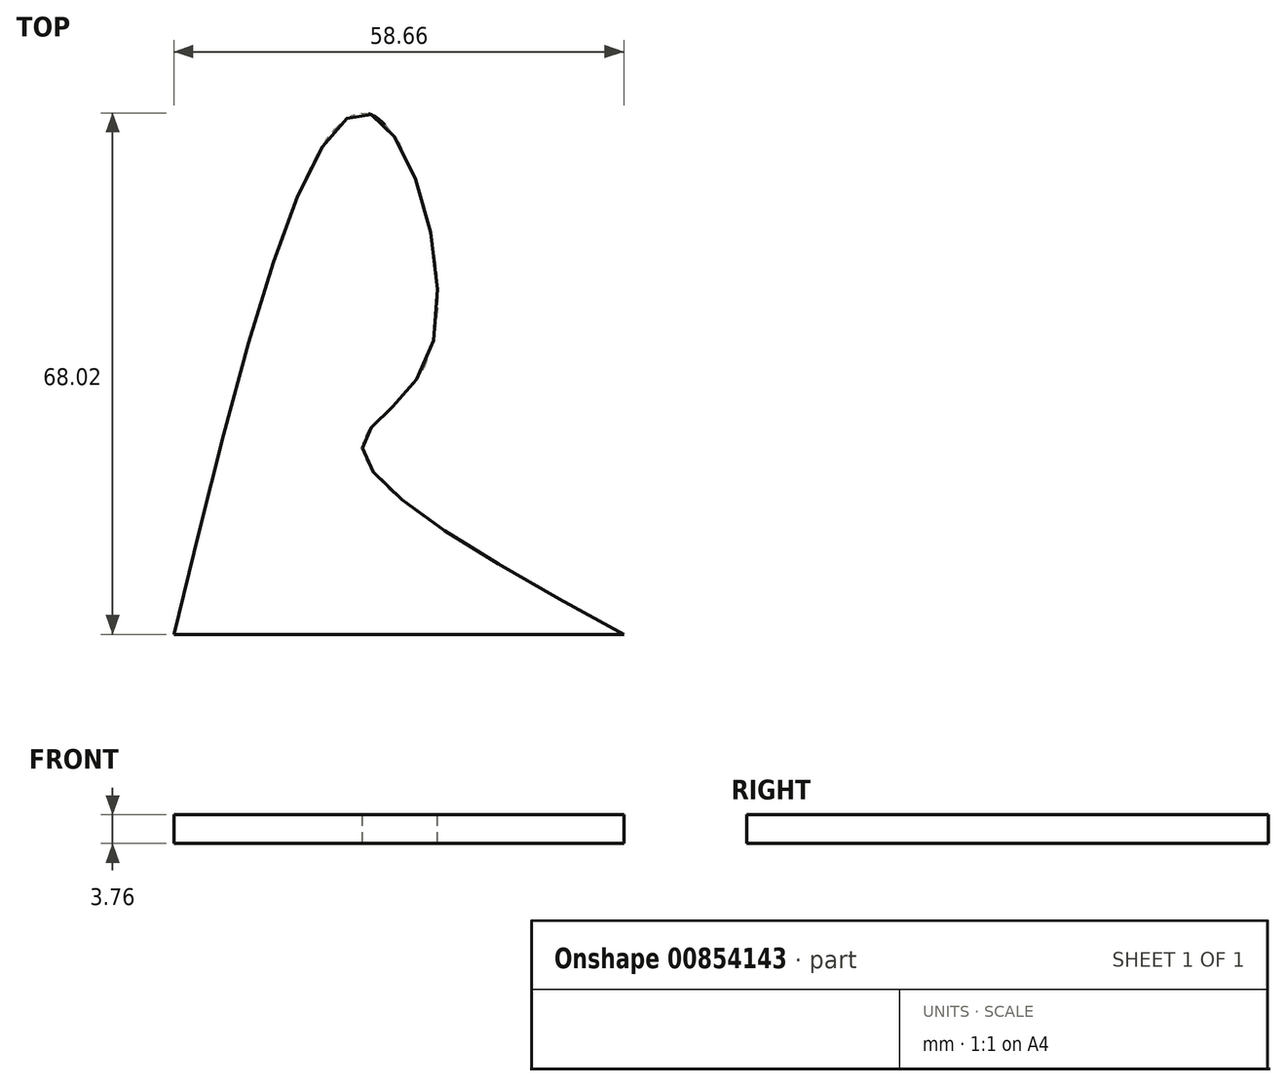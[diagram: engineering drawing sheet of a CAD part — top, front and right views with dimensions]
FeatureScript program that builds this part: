
annotation { "Feature Type Name" : "Feature", "Feature Type Description" : "" }
export const myFeature = defineFeature(function(context is Context, id is Id, definition is map)
    precondition{}
    {
        {
            var Q0;
            Q0=qCreatedBy(makeId("Top.planeOp"),FACE);
            var sketch = newSketch(context, id + "F0", { "sketchPlane" : qUnion([Q0])});
            skLineSegment(sketch, "E0", {"start": v(-58.66, -79.08) * mm, "end": v(0, -79.08) * mm});
            skFitSpline(sketch, "E1", {"points": [v(-58.66, -79.08) * mm, v(-33, -11.27) * mm, v(-25.3, -42.48) * mm, v(-34.1, -54.52) * mm, v(0, -79.08) * mm], "startDerivative": vector(74.69, 307.11) * mm, "endDerivative": vector(195.08, -107.07) * mm});
            skSolve(sketch);
        }
        {
            var Q0;
            Q0 = qSketchRegion(id + "F0", true);
            var Q1;
            Q1=makeQuery(id+"F0.imprint","IMPRINT",FACE,{"disambiguationData":[TD([[makeQuery(id+"F0.imprint","IMPRINT",EDGE,{"derivedFrom":sQuery(id+"F0.wireOp",EDGE,"E0")}),1.0]])]});
            extrude(context, id + "F1", {"entities" : qUnion([Q0, Q1]), "depth" : 3.76 * mm, "offsetDistance" : 25.4 * mm});
        }
    });
